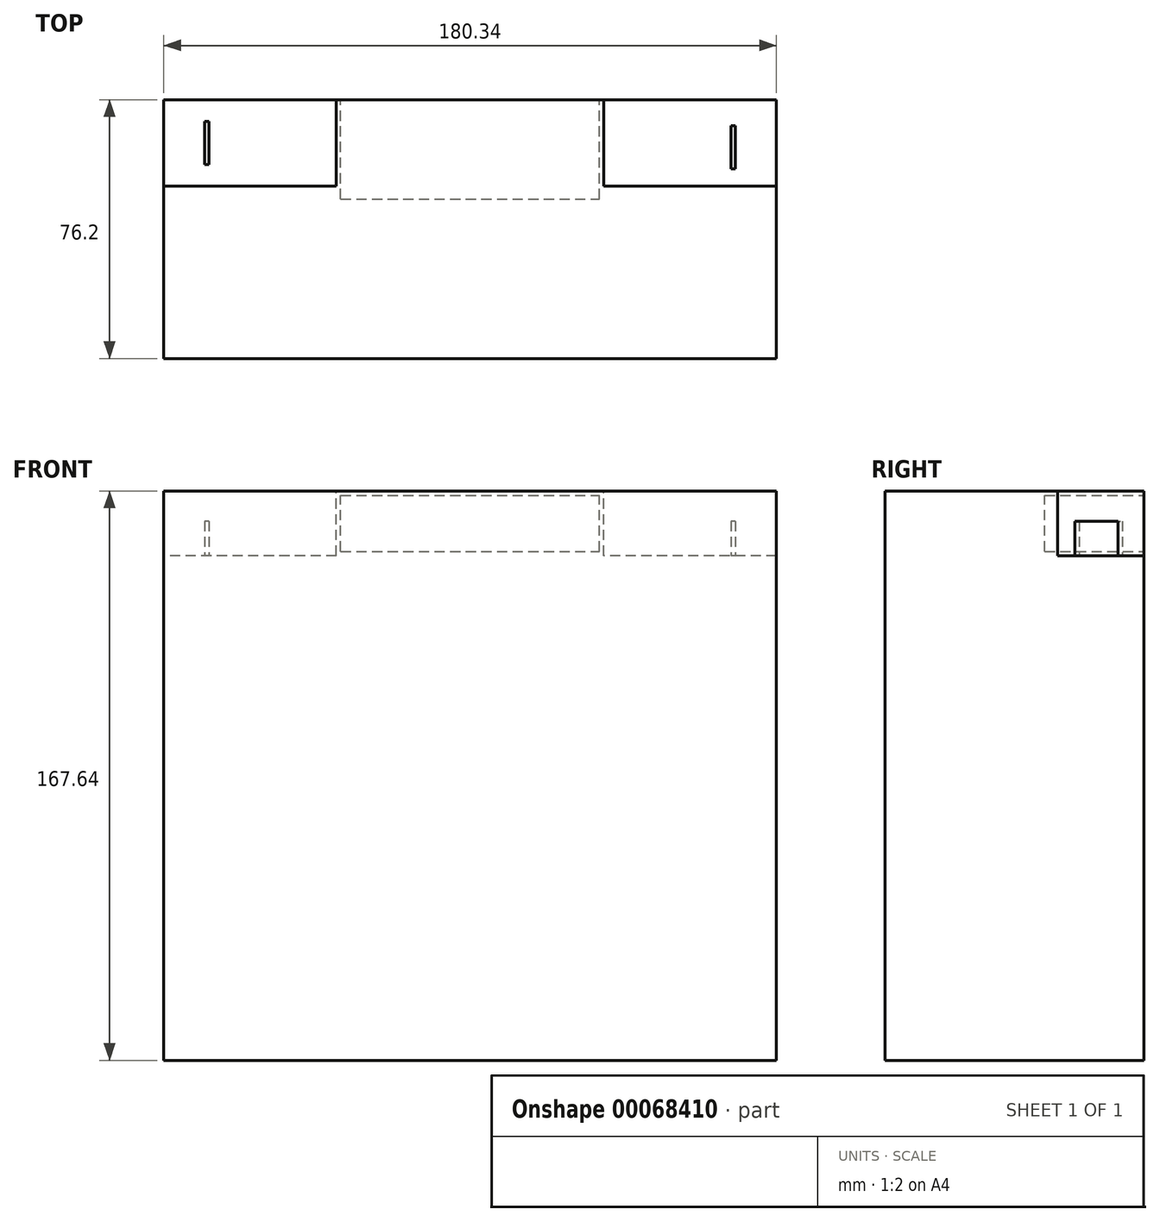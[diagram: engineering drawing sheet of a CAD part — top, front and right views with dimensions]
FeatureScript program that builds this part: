
annotation { "Feature Type Name" : "Feature", "Feature Type Description" : "" }
export const myFeature = defineFeature(function(context is Context, id is Id, definition is map)
    precondition{}
    {
        {
            var Q0;
            Q0=qCreatedBy(makeId("Top.planeOp"),FACE);
            var sketch = newSketch(context, id + "F0", { "sketchPlane" : qUnion([Q0])});
            skLineSegment(sketch, "E0.rect.bottom", {"start": v(90.17, -38.1) * mm, "end": v(-90.17, -38.1) * mm});
            skLineSegment(sketch, "E0.rect.top", {"start": v(90.17, 38.1) * mm, "end": v(-90.17, 38.1) * mm});
            skLineSegment(sketch, "E0.rect.left", {"start": v(90.17, -38.1) * mm, "end": v(90.17, 38.1) * mm});
            skLineSegment(sketch, "E0.rect.right", {"start": v(-90.17, -38.1) * mm, "end": v(-90.17, 38.1) * mm});
            skPoint(sketch, "E0.rect.middle", {"position": v(0, 0) * mm});
            skSolve(sketch);
        }
        {
            var Q0;
            Q0=makeQuery(id+"F0.imprint","IMPRINT",FACE,{"disambiguationData":[TD([[makeQuery(id+"F0.imprint","IMPRINT",EDGE,{"derivedFrom":sQuery(id+"F0.wireOp",EDGE,"E0.rect.bottom")}),-1.0]])]});
            extrude(context, id + "F1", {"entities" : qUnion([Q0]), "depth" : 167.64 * mm});
        }
        {
            var Q0;
            Q0=makeQuery(id+"F1.opExtrude","CAP_FACE",FACE,{"disambiguationData":[OSD([sQuery(id+"F0.wireOp",EDGE,"E0.rect.bottom"),sQuery(id+"F0.wireOp",EDGE,"E0.rect.top"),sQuery(id+"F0.wireOp",EDGE,"E0.rect.left"),sQuery(id+"F0.wireOp",EDGE,"E0.rect.right")])],"isStart":false});
            var sketch = newSketch(context, id + "F2", { "sketchPlane" : qUnion([Q0])});
            skLineSegment(sketch, "E1.bottom", {"start": v(90.17, 38.1) * mm, "end": v(39.37, 38.1) * mm});
            skLineSegment(sketch, "E1.top", {"start": v(90.17, 12.7) * mm, "end": v(39.37, 12.7) * mm});
            skLineSegment(sketch, "E1.left", {"start": v(90.17, 38.1) * mm, "end": v(90.17, 12.7) * mm});
            skLineSegment(sketch, "E1.right", {"start": v(39.37, 38.1) * mm, "end": v(39.37, 12.7) * mm});
            skLineSegment(sketch, "E2.bottom", {"start": v(-90.17, 38.1) * mm, "end": v(-39.37, 38.1) * mm});
            skLineSegment(sketch, "E2.top", {"start": v(-90.17, 12.7) * mm, "end": v(-39.37, 12.7) * mm});
            skLineSegment(sketch, "E2.left", {"start": v(-90.17, 38.1) * mm, "end": v(-90.17, 12.7) * mm});
            skLineSegment(sketch, "E2.right", {"start": v(-39.37, 38.1) * mm, "end": v(-39.37, 12.7) * mm});
            skSolve(sketch);
        }
        {
            var Q0;
            Q0=makeQuery(id+"F2.imprint","IMPRINT",FACE,{"disambiguationData":[TD([[makeQuery(id+"F2.imprint","IMPRINT",EDGE,{"derivedFrom":sQuery(id+"F2.wireOp",EDGE,"E1.bottom")}),1.0]])]});
            var Q1;
            Q1=makeQuery(id+"F2.imprint","IMPRINT",FACE,{"disambiguationData":[TD([[makeQuery(id+"F2.imprint","IMPRINT",EDGE,{"derivedFrom":sQuery(id+"F2.wireOp",EDGE,"E2.bottom")}),1.0]])]});
            extrude(context, id + "F3", {"entities" : qUnion([Q0, Q1]), "operationType" : NewBodyOperationType.REMOVE, "oppositeDirection" : true, "depth" : 19.05 * mm});
        }
        {
            var Q0;
            Q0=makeQuery(id+"F3.boolean.opBoolean","COPY",FACE,{"derivedFrom":makeQuery(id+"F3.opExtrude","CAP_FACE",FACE,{"disambiguationData":[OSD([sQuery(id+"F2.wireOp",EDGE,"E2.bottom"),sQuery(id+"F2.wireOp",EDGE,"E2.top"),sQuery(id+"F2.wireOp",EDGE,"E2.left"),sQuery(id+"F2.wireOp",EDGE,"E2.right")])],"isStart":false})});
            var sketch = newSketch(context, id + "F4", { "sketchPlane" : qUnion([Q0])});
            skLineSegment(sketch, "E3.rect.bottom", {"start": v(78.1, 17.7) * mm, "end": v(76.84, 17.7) * mm});
            skLineSegment(sketch, "E3.rect.top", {"start": v(78.1, 30.4) * mm, "end": v(76.84, 30.4) * mm});
            skLineSegment(sketch, "E3.rect.left", {"start": v(78.1, 17.7) * mm, "end": v(78.1, 30.4) * mm});
            skLineSegment(sketch, "E3.rect.right", {"start": v(76.84, 17.7) * mm, "end": v(76.84, 30.4) * mm});
            skPoint(sketch, "E3.rect.middle", {"position": v(77.47, 24.04) * mm});
            skLineSegment(sketch, "E4.rect.bottom", {"start": v(-76.83, 18.99) * mm, "end": v(-78.1, 18.99) * mm});
            skLineSegment(sketch, "E4.rect.top", {"start": v(-76.83, 31.69) * mm, "end": v(-78.1, 31.69) * mm});
            skLineSegment(sketch, "E4.rect.left", {"start": v(-76.83, 18.99) * mm, "end": v(-76.83, 31.69) * mm});
            skLineSegment(sketch, "E4.rect.right", {"start": v(-78.1, 18.99) * mm, "end": v(-78.1, 31.69) * mm});
            skPoint(sketch, "E4.rect.middle", {"position": v(-77.47, 25.34) * mm});
            skSolve(sketch);
        }
        {
            var Q0;
            Q0=makeQuery(id+"F4.imprint","IMPRINT",FACE,{"disambiguationData":[TD([[makeQuery(id+"F4.imprint","IMPRINT",EDGE,{"derivedFrom":sQuery(id+"F4.wireOp",EDGE,"E3.rect.bottom")}),-1.0]])]});
            var Q1;
            Q1=makeQuery(id+"F4.imprint","IMPRINT",FACE,{"disambiguationData":[TD([[makeQuery(id+"F4.imprint","IMPRINT",EDGE,{"derivedFrom":sQuery(id+"F4.wireOp",EDGE,"E4.rect.bottom")}),-1.0]])]});
            extrude(context, id + "F5", {"entities" : qUnion([Q0, Q1]), "operationType" : NewBodyOperationType.ADD, "depth" : 10.16 * mm});
        }
        {
            var Q0;
            Q0=makeQuery(id+"F1.opExtrude","SWEPT_FACE",FACE,{"disambiguationData":[OSD([sQuery(id+"F0.wireOp",EDGE,"E0.rect.top")])]});
            var sketch = newSketch(context, id + "F6", { "sketchPlane" : qUnion([Q0])});
            skLineSegment(sketch, "E5", {"start": v(-39.37, 148.6) * mm, "end": v(39.37, 148.6) * mm});
            skSolve(sketch);
        }
        {
            var Q0;
            Q0=makeQuery(id+"F6.imprint","IMPRINT",FACE,{"disambiguationData":[TD([[makeQuery(id+"F6.imprint","IMPRINT",EDGE,{"derivedFrom":sQuery(id+"F6.wireOp",EDGE,"E5")}),1.0]])]});
            var sketch = newSketch(context, id + "F7", { "sketchPlane" : qUnion([Q0])});
            skLineSegment(sketch, "E6.rect.bottom", {"start": v(38.1, 149.86) * mm, "end": v(-38.1, 149.86) * mm});
            skLineSegment(sketch, "E6.rect.top", {"start": v(38.1, 166.37) * mm, "end": v(-38.1, 166.37) * mm});
            skLineSegment(sketch, "E6.rect.left", {"start": v(38.1, 149.86) * mm, "end": v(38.1, 166.37) * mm});
            skLineSegment(sketch, "E6.rect.right", {"start": v(-38.1, 149.86) * mm, "end": v(-38.1, 166.37) * mm});
            skPoint(sketch, "E6.rect.middle", {"position": v(0, 158.12) * mm});
            skSolve(sketch);
        }
        {
            var Q0;
            Q0=makeQuery(id+"F7.imprint","IMPRINT",FACE,{"disambiguationData":[TD([[makeQuery(id+"F7.imprint","IMPRINT",EDGE,{"derivedFrom":sQuery(id+"F7.wireOp",EDGE,"E6.rect.bottom")}),-1.0]])]});
            extrude(context, id + "F8", {"entities" : qUnion([Q0]), "operationType" : NewBodyOperationType.REMOVE, "oppositeDirection" : true, "depth" : 29.24 * mm});
        }
    });
